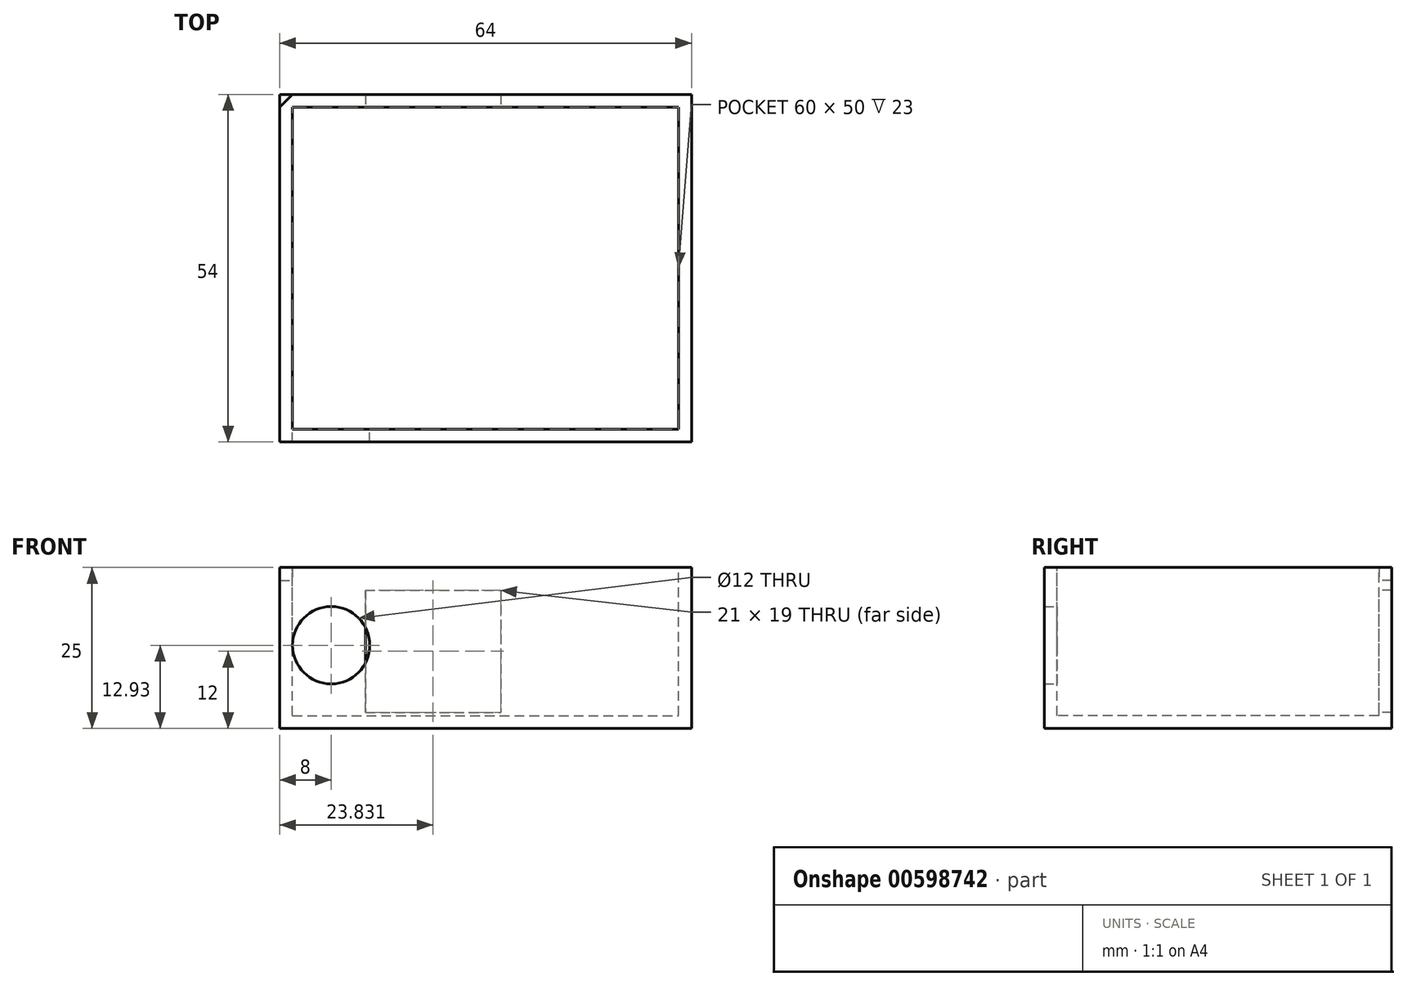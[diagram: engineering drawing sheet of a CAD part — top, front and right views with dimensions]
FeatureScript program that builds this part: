
annotation { "Feature Type Name" : "Feature", "Feature Type Description" : "" }
export const myFeature = defineFeature(function(context is Context, id is Id, definition is map)
    precondition{}
    {
        {
            var Q0;
            Q0=qCreatedBy(makeId("Top.planeOp"),FACE);
            var sketch = newSketch(context, id + "F0", { "sketchPlane" : qUnion([Q0])});
            skLineSegment(sketch, "E0.bottom", {"start": v(-32, 27) * mm, "end": v(32, 27) * mm});
            skLineSegment(sketch, "E0.top", {"start": v(-32, -27) * mm, "end": v(32, -27) * mm});
            skLineSegment(sketch, "E0.left", {"start": v(-32, 27) * mm, "end": v(-32, -27) * mm});
            skLineSegment(sketch, "E0.right", {"start": v(32, 27) * mm, "end": v(32, -27) * mm});
            skPoint(sketch, "E0.middle", {"position": v(0, 0) * mm});
            skSolve(sketch);
        }
        {
            var Q0;
            Q0=makeQuery(id+"F0.imprint","IMPRINT",FACE,{"disambiguationData":[TD([[makeQuery(id+"F0.imprint","IMPRINT",EDGE,{"derivedFrom":sQuery(id+"F0.wireOp",EDGE,"E0.bottom")}),-1.0]])]});
            extrude(context, id + "F1", {"entities" : qUnion([Q0]), "depth" : 23 * mm, "offsetDistance" : 25.4 * mm});
        }
        {
            var Q0;
            Q0=makeQuery(id+"F1.opExtrude","CAP_FACE",FACE,{"disambiguationData":[OSD([sQuery(id+"F0.wireOp",EDGE,"E0.bottom"),sQuery(id+"F0.wireOp",EDGE,"E0.top"),sQuery(id+"F0.wireOp",EDGE,"E0.left"),sQuery(id+"F0.wireOp",EDGE,"E0.right")])],"isStart":false});
            var sketch = newSketch(context, id + "F2", { "sketchPlane" : qUnion([Q0])});
            skLineSegment(sketch, "E1.bottom", {"start": v(-30, 25) * mm, "end": v(30, 25) * mm});
            skLineSegment(sketch, "E1.top", {"start": v(-30, -25) * mm, "end": v(30, -25) * mm});
            skLineSegment(sketch, "E1.left", {"start": v(-30, 25) * mm, "end": v(-30, -25) * mm});
            skLineSegment(sketch, "E1.right", {"start": v(30, 25) * mm, "end": v(30, -25) * mm});
            skPoint(sketch, "E1.middle", {"position": v(0, 0) * mm});
            skSolve(sketch);
        }
        {
            var Q0;
            Q0 = qSketchRegion(id + "F2", true);
            extrude(context, id + "F3", {"entities" : qUnion([Q0]), "operationType" : NewBodyOperationType.REMOVE, "oppositeDirection" : true, "depth" : 21 * mm, "offsetDistance" : 25.4 * mm});
        }
        {
            var Q0;
            Q0=makeQuery(id+"F3.boolean.opBoolean","COPY",FACE,{"derivedFrom":makeQuery(id+"F3.opExtrude","SWEPT_FACE",FACE,{"disambiguationData":[OSD([sQuery(id+"F2.wireOp",EDGE,"E1.top")])]})});
            var sketch = newSketch(context, id + "F4", { "sketchPlane" : qUnion([Q0])});
            skLineSegment(sketch, "E2.bottom", {"start": v(30, 2) * mm, "end": v(18, 2) * mm});
            skLineSegment(sketch, "E2.top", {"start": v(30, 18.93) * mm, "end": v(18, 18.93) * mm});
            skLineSegment(sketch, "E2.left", {"start": v(30, 2) * mm, "end": v(30, 18.93) * mm});
            skLineSegment(sketch, "E2.right", {"start": v(18, 2) * mm, "end": v(18, 18.93) * mm});
            skLineSegment(sketch, "E3.bottom", {"start": v(18, 18.93) * mm, "end": v(30, 18.93) * mm});
            skLineSegment(sketch, "E3.top", {"start": v(18, 6.93) * mm, "end": v(30, 6.93) * mm});
            skLineSegment(sketch, "E3.left", {"start": v(18, 18.93) * mm, "end": v(18, 6.93) * mm});
            skLineSegment(sketch, "E3.right", {"start": v(30, 18.93) * mm, "end": v(30, 6.93) * mm});
            skCircle(sketch, "E4", {"center": v(24, 12.93) * mm, "radius": 6 * mm});
            skPoint(sketch, "E4.first.point", {"position": v(24, 18.93) * mm});
            skPoint(sketch, "E4.second.point", {"position": v(24, 6.93) * mm});
            skPoint(sketch, "E4.third.point", {"position": v(18, 12.93) * mm});
            skSolve(sketch);
        }
        {
            var Q0;
            {var subQ0=sQuery(id+"F4.wireOp",EDGE,"E4");var subQ1=makeQuery(id+"F4.imprint","INTERSECT",VERTEX,{"derivedFrom":[sQuery(id+"F4.wireOp",EDGE,"E3.right"),subQ0]});Q0=makeQuery(id+"F4.imprint","IMPRINT",FACE,{"disambiguationData":[TD([[makeQuery(id+"F4.imprint","IMPRINT",EDGE,{"disambiguationData":[TD([[subQ1,-1.0]])],"derivedFrom":subQ0}),1.0]])]});}
            extrude(context, id + "F5", {"entities" : qUnion([Q0]), "operationType" : NewBodyOperationType.REMOVE, "oppositeDirection" : true, "depth" : 25.4 * mm, "offsetDistance" : 25.4 * mm, "hasSecondDirection" : true, "secondDirectionOppositeDirection" : false, "secondDirectionDepth" : 25.4 * mm});
        }
        {
            var Q0;
            Q0=makeQuery(id+"F3.boolean.opBoolean","COPY",FACE,{"derivedFrom":makeQuery(id+"F3.opExtrude","SWEPT_FACE",FACE,{"disambiguationData":[OSD([sQuery(id+"F2.wireOp",EDGE,"E1.bottom")])]})});
            var sketch = newSketch(context, id + "F6", { "sketchPlane" : qUnion([Q0])});
            skLineSegment(sketch, "E5", {"start": v(-8.17, 2) * mm, "end": v(-8.17, 12) * mm});
            skLineSegment(sketch, "E6.bottom", {"start": v(2.33, 2.5) * mm, "end": v(-18.67, 2.5) * mm});
            skLineSegment(sketch, "E6.top", {"start": v(2.33, 21.5) * mm, "end": v(-18.67, 21.5) * mm});
            skLineSegment(sketch, "E6.left", {"start": v(2.33, 2.5) * mm, "end": v(2.33, 21.5) * mm});
            skLineSegment(sketch, "E6.right", {"start": v(-18.67, 2.5) * mm, "end": v(-18.67, 21.5) * mm});
            skPoint(sketch, "E6.middle", {"position": v(-8.17, 12) * mm});
            skSolve(sketch);
        }
        {
            var Q0;
            Q0=makeQuery(id+"F6.imprint","IMPRINT",FACE,{"disambiguationData":[TD([[makeQuery(id+"F6.imprint","IMPRINT",EDGE,{"derivedFrom":sQuery(id+"F6.wireOp",EDGE,"E6.top")}),1.0]])]});
            extrude(context, id + "F7", {"entities" : qUnion([Q0]), "operationType" : NewBodyOperationType.REMOVE, "oppositeDirection" : true, "depth" : 25.4 * mm, "offsetDistance" : 25.4 * mm, "hasSecondDirection" : true, "secondDirectionOppositeDirection" : false, "secondDirectionDepth" : 25.4 * mm});
        }
        {
            var Q0;
            Q0=makeQuery(id+"F3.boolean.opBoolean","COPY",FACE,{"derivedFrom":makeQuery(id+"F3.opExtrude","CAP_FACE",FACE,{"disambiguationData":[OSD([sQuery(id+"F2.wireOp",EDGE,"E1.bottom"),sQuery(id+"F2.wireOp",EDGE,"E1.top"),sQuery(id+"F2.wireOp",EDGE,"E1.left"),sQuery(id+"F2.wireOp",EDGE,"E1.right")])],"isStart":false})});
            var sketch = newSketch(context, id + "F8", { "sketchPlane" : qUnion([Q0])});
            skLineSegment(sketch, "E7", {"start": v(-30, -25) * mm, "end": v(-30, 5) * mm});
            skPoint(sketch, "E8", {"position": v(-30, 5) * mm});
            skLineSegment(sketch, "E9", {"start": v(30, -25) * mm, "end": v(-2.5, -25) * mm});
            skLineSegment(sketch, "E10", {"start": v(30, 25) * mm, "end": v(30, 10.86) * mm});
            skLineSegment(sketch, "E11", {"start": v(30, 10.86) * mm, "end": v(30, -21.64) * mm});
            skLineSegment(sketch, "E12", {"start": v(30, 25) * mm, "end": v(15.86, 25) * mm});
            skPoint(sketch, "E13", {"position": v(-2.5, -21.64) * mm});
            skPoint(sketch, "E14", {"position": v(30, 10.86) * mm});
            skSolve(sketch);
        }
        {
            var Q0;
            Q0=makeQuery(id+"F1.opExtrude","CAP_FACE",FACE,{"disambiguationData":[OSD([sQuery(id+"F0.wireOp",EDGE,"E0.bottom"),sQuery(id+"F0.wireOp",EDGE,"E0.top"),sQuery(id+"F0.wireOp",EDGE,"E0.left"),sQuery(id+"F0.wireOp",EDGE,"E0.right")])],"isStart":true});
            var sketch = newSketch(context, id + "F9", { "sketchPlane" : qUnion([Q0])});
            skLineSegment(sketch, "E15", {"start": v(32, -27) * mm, "end": v(20, -27) * mm});
            skLineSegment(sketch, "E16", {"start": v(20, -27) * mm, "end": v(-20, -27) * mm});
            skSolve(sketch);
        }
        {
            var Q0;
            Q0=makeQuery(id+"F1.opExtrude","CAP_FACE",FACE,{"disambiguationData":[OSD([sQuery(id+"F0.wireOp",EDGE,"E0.bottom"),sQuery(id+"F0.wireOp",EDGE,"E0.top"),sQuery(id+"F0.wireOp",EDGE,"E0.left"),sQuery(id+"F0.wireOp",EDGE,"E0.right")])],"isStart":false});
            var sketch = newSketch(context, id + "F10", { "sketchPlane" : qUnion([Q0])});
            skLineSegment(sketch, "E17", {"start": v(-32, 27) * mm, "end": v(-30, 25) * mm});
            skLineSegment(sketch, "E18", {"start": v(-30, 25) * mm, "end": v(-30, 27) * mm});
            skLineSegment(sketch, "E19", {"start": v(-30, 27) * mm, "end": v(-32, 25) * mm});
            skPoint(sketch, "E20", {"position": v(-31, 26) * mm});
            skCircle(sketch, "E21", {"center": v(-31, 26) * mm, "radius": 0.5 * mm});
            skSolve(sketch);
        }
        {
            var Q0;
            {var subQ0=sQuery(id+"F10.wireOp",EDGE,"E19");var subQ1=sQuery(id+"F10.wireOp",EDGE,"E17");var subQ2=makeQuery(id+"F10.imprint","INTERSECT",VERTEX,{"derivedFrom":[subQ1,subQ0]});Q0=makeQuery(id+"F10.imprint","IMPRINT",FACE,{"disambiguationData":[TD([[makeQuery(id+"F10.imprint","IMPRINT",EDGE,{"disambiguationData":[TD([[subQ2,-1.0]])],"derivedFrom":subQ1}),1.0]])]});}
            var Q1;
            {var subQ0=sQuery(id+"F10.wireOp",EDGE,"E21");var subQ1=sQuery(id+"F10.wireOp",EDGE,"E17");var subQ2=makeQuery(id+"F10.imprint","INTERSECT",VERTEX,{"disambiguationData":[OD(0.0)],"derivedFrom":[subQ1,subQ0]});Q1=makeQuery(id+"F10.imprint","IMPRINT",FACE,{"disambiguationData":[TD([[makeQuery(id+"F10.imprint","IMPRINT",EDGE,{"disambiguationData":[TD([[subQ2,-1.0]])],"derivedFrom":subQ1}),1.0]])]});}
            var Q2;
            {var subQ0=sQuery(id+"F10.wireOp",EDGE,"E21");var subQ1=sQuery(id+"F10.wireOp",EDGE,"E17");var subQ2=makeQuery(id+"F10.imprint","INTERSECT",VERTEX,{"disambiguationData":[OD(0.0)],"derivedFrom":[subQ1,subQ0]});Q2=makeQuery(id+"F10.imprint","IMPRINT",FACE,{"disambiguationData":[TD([[makeQuery(id+"F10.imprint","IMPRINT",EDGE,{"disambiguationData":[TD([[subQ2,-1.0]])],"derivedFrom":subQ1}),-1.0]])]});}
            var Q3;
            {var subQ0=sQuery(id+"F10.wireOp",EDGE,"E19");var subQ1=sQuery(id+"F10.wireOp",EDGE,"E17");var subQ2=makeQuery(id+"F10.imprint","INTERSECT",VERTEX,{"derivedFrom":[subQ1,subQ0]});Q3=makeQuery(id+"F10.imprint","IMPRINT",FACE,{"disambiguationData":[TD([[makeQuery(id+"F10.imprint","IMPRINT",EDGE,{"disambiguationData":[TD([[subQ2,-1.0]])],"derivedFrom":subQ1}),-1.0]])]});}
            extrude(context, id + "F11", {"entities" : qUnion([Q0, Q1, Q2, Q3]), "operationType" : NewBodyOperationType.ADD, "depth" : 2 * mm, "offsetDistance" : 25.4 * mm});
        }
        {
            var Q0;
            Q0=makeQuery(id+"F1.opExtrude","CAP_FACE",FACE,{"disambiguationData":[OSD([sQuery(id+"F0.wireOp",EDGE,"E0.bottom"),sQuery(id+"F0.wireOp",EDGE,"E0.top"),sQuery(id+"F0.wireOp",EDGE,"E0.left"),sQuery(id+"F0.wireOp",EDGE,"E0.right")])],"isStart":false});
            var sketch = newSketch(context, id + "F12", { "sketchPlane" : qUnion([Q0])});
            skLineSegment(sketch, "E22", {"start": v(30, -25) * mm, "end": v(32, -27) * mm});
            skLineSegment(sketch, "E23", {"start": v(32, -27) * mm, "end": v(32, -25) * mm});
            skLineSegment(sketch, "E24", {"start": v(32, -25) * mm, "end": v(30, -27) * mm});
            skPoint(sketch, "E25", {"position": v(31, -26) * mm});
            skCircle(sketch, "E26", {"center": v(31, -26) * mm, "radius": 0.5 * mm});
            skSolve(sketch);
        }
        {
            var Q0;
            {var subQ0=sQuery(id+"F12.wireOp",EDGE,"E26");var subQ1=sQuery(id+"F12.wireOp",EDGE,"E22");var subQ2=makeQuery(id+"F12.imprint","INTERSECT",VERTEX,{"disambiguationData":[OD(0.0)],"derivedFrom":[subQ1,subQ0]});Q0=makeQuery(id+"F12.imprint","IMPRINT",FACE,{"disambiguationData":[TD([[makeQuery(id+"F12.imprint","IMPRINT",EDGE,{"disambiguationData":[TD([[subQ2,-1.0]])],"derivedFrom":subQ1}),-1.0]])]});}
            var Q1;
            {var subQ0=sQuery(id+"F12.wireOp",EDGE,"E26");var subQ1=sQuery(id+"F12.wireOp",EDGE,"E22");var subQ2=makeQuery(id+"F12.imprint","INTERSECT",VERTEX,{"disambiguationData":[OD(0.0)],"derivedFrom":[subQ1,subQ0]});Q1=makeQuery(id+"F12.imprint","IMPRINT",FACE,{"disambiguationData":[TD([[makeQuery(id+"F12.imprint","IMPRINT",EDGE,{"disambiguationData":[TD([[subQ2,-1.0]])],"derivedFrom":subQ1}),1.0]])]});}
            var Q2;
            {var subQ0=sQuery(id+"F12.wireOp",EDGE,"E24");var subQ1=sQuery(id+"F12.wireOp",EDGE,"E22");var subQ2=makeQuery(id+"F12.imprint","INTERSECT",VERTEX,{"derivedFrom":[subQ1,subQ0]});Q2=makeQuery(id+"F12.imprint","IMPRINT",FACE,{"disambiguationData":[TD([[makeQuery(id+"F12.imprint","IMPRINT",EDGE,{"disambiguationData":[TD([[subQ2,-1.0]])],"derivedFrom":subQ1}),1.0]])]});}
            var Q3;
            {var subQ0=sQuery(id+"F12.wireOp",EDGE,"E24");var subQ1=sQuery(id+"F12.wireOp",EDGE,"E22");var subQ2=makeQuery(id+"F12.imprint","INTERSECT",VERTEX,{"derivedFrom":[subQ1,subQ0]});Q3=makeQuery(id+"F12.imprint","IMPRINT",FACE,{"disambiguationData":[TD([[makeQuery(id+"F12.imprint","IMPRINT",EDGE,{"disambiguationData":[TD([[subQ2,-1.0]])],"derivedFrom":subQ1}),-1.0]])]});}
            extrude(context, id + "F13", {"entities" : qUnion([Q0, Q1, Q2, Q3]), "operationType" : NewBodyOperationType.ADD, "depth" : 2 * mm, "offsetDistance" : 25.4 * mm});
        }
    });
